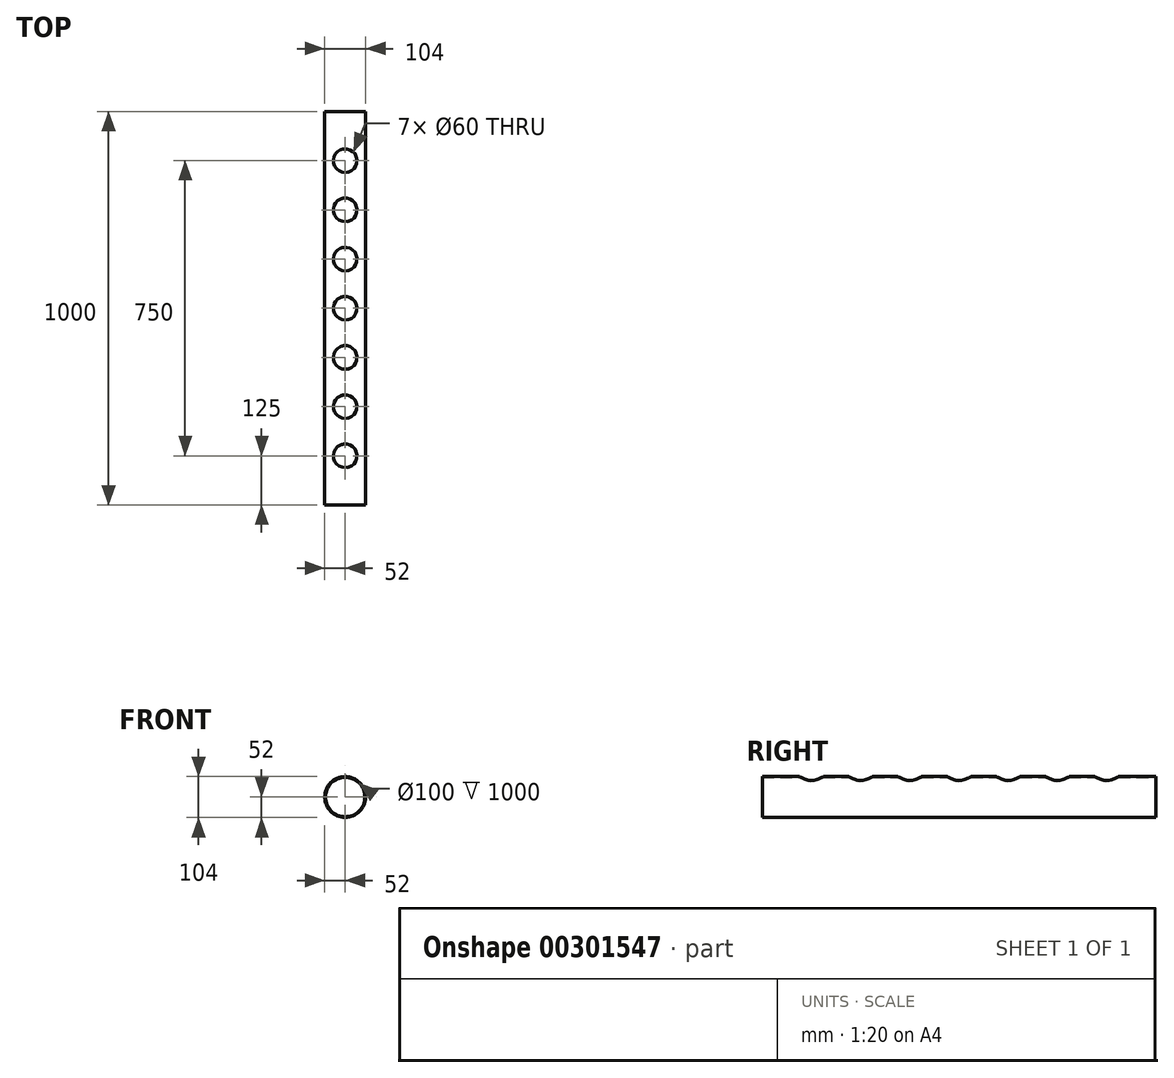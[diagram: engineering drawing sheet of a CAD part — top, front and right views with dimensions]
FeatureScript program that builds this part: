
annotation { "Feature Type Name" : "Feature", "Feature Type Description" : "" }
export const myFeature = defineFeature(function(context is Context, id is Id, definition is map)
    precondition{}
    {
        {
            var Q0;
            Q0=qCreatedBy(makeId("Front.planeOp"),FACE);
            var sketch = newSketch(context, id + "F0", { "sketchPlane" : qUnion([Q0])});
            skCircle(sketch, "E0", {"center": v(0, 0) * mm, "radius": 52 * mm});
            skCircle(sketch, "E1", {"center": v(0, 0) * mm, "radius": 50 * mm});
            skSolve(sketch);
        }
        {
            var Q0;
            Q0 = qSketchRegion(id + "F0", true);
            extrude(context, id + "F1", {"entities" : qUnion([Q0]), "depth" : 1000 * mm});
        }
        {
            var Q0;
            Q0=qCreatedBy(makeId("Top.planeOp"),FACE);
            var sketch = newSketch(context, id + "F2", { "sketchPlane" : qUnion([Q0])});
            skCircle(sketch, "E2", {"center": v(0, -125) * mm, "radius": 30 * mm});
            skCircle(sketch, "E3.0.1.0", {"center": v(0, -250) * mm, "radius": 30 * mm});
            skCircle(sketch, "E3.0.2.0", {"center": v(0, -375) * mm, "radius": 30 * mm});
            skCircle(sketch, "E3.0.3.0", {"center": v(0, -500) * mm, "radius": 30 * mm});
            skCircle(sketch, "E3.0.4.0", {"center": v(0, -625) * mm, "radius": 30 * mm});
            skCircle(sketch, "E3.0.5.0", {"center": v(0, -750) * mm, "radius": 30 * mm});
            skLineSegment(sketch, "E3.direction1", {"start": v(0, -125) * mm, "end": v(-440, -125) * mm, "construction": true});
            skLineSegment(sketch, "E3.direction2", {"start": v(0, -125) * mm, "end": v(0, -250) * mm, "construction": true});
            skCircle(sketch, "E4.0.0.6", {"center": v(0, -875) * mm, "radius": 30 * mm});
            skCircle(sketch, "E4.0.1.6", {"center": v(-440, -875) * mm, "radius": 30 * mm});
            skCircle(sketch, "E4.0.2.6", {"center": v(-880, -875) * mm, "radius": 30 * mm});
            skSolve(sketch);
        }
        {
            var Q0;
            Q0 = qSketchRegion(id + "F2", true);
            extrude(context, id + "F3", {"entities" : qUnion([Q0]), "operationType" : NewBodyOperationType.REMOVE, "depth" : 100 * mm});
        }
    });
